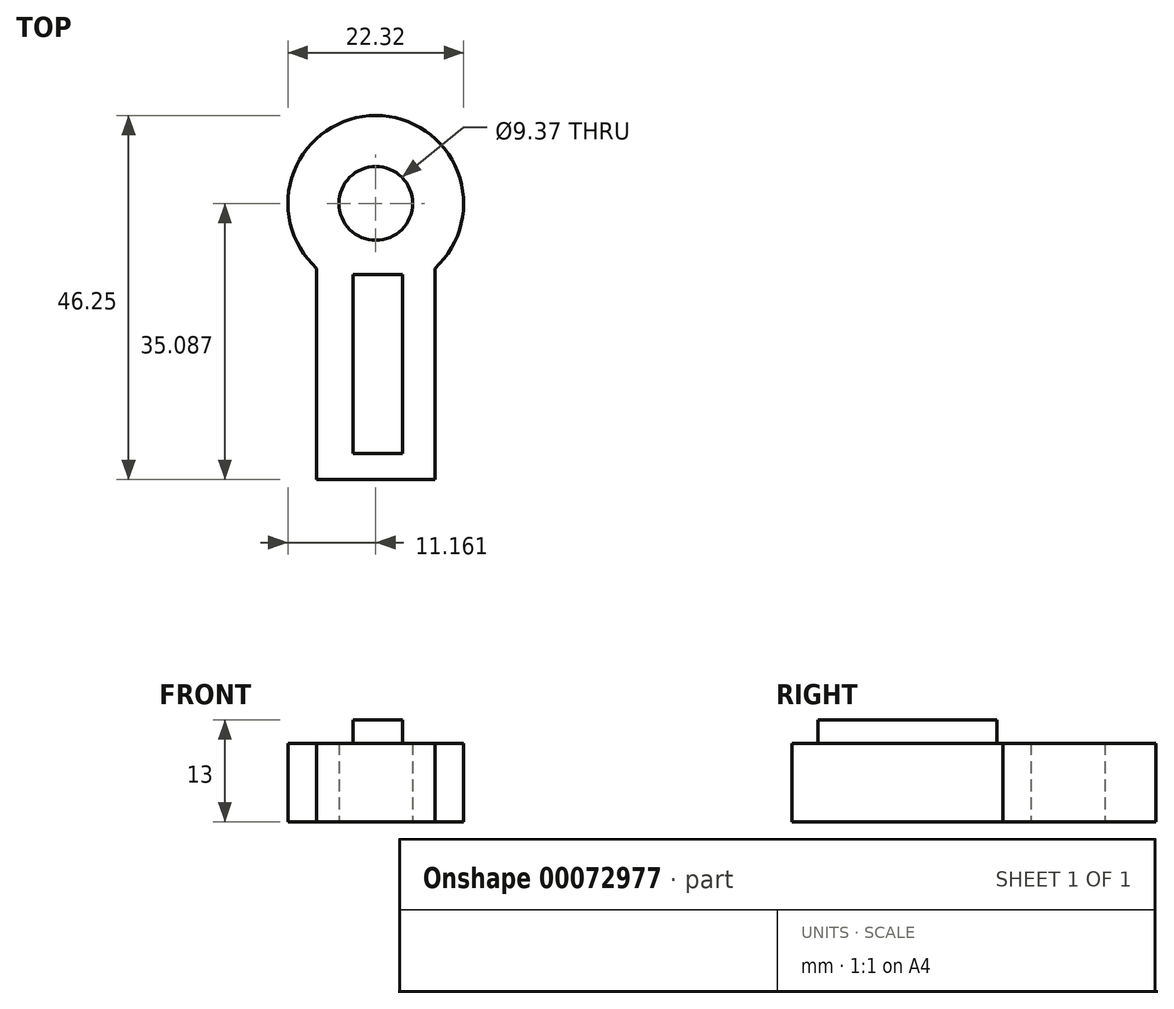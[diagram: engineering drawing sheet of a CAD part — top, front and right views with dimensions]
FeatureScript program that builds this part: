
annotation { "Feature Type Name" : "Feature", "Feature Type Description" : "" }
export const myFeature = defineFeature(function(context is Context, id is Id, definition is map)
    precondition{}
    {
        {
            var Q0;
            Q0=qCreatedBy(makeId("Top.planeOp"),FACE);
            var sketch = newSketch(context, id + "F0", { "sketchPlane" : qUnion([Q0])});
            skArc(sketch, "E0", {"start": v(20.52, 31.4) * mm, "mid": v(13.02, 50.82) * mm, "end": v(5.52, 31.4) * mm});
            skLineSegment(sketch, "E1.top", {"start": v(5.52, 4.57) * mm, "end": v(20.52, 4.57) * mm});
            skLineSegment(sketch, "E1.left", {"start": v(5.52, 31.4) * mm, "end": v(5.52, 4.57) * mm});
            skLineSegment(sketch, "E1.right", {"start": v(20.52, 31.4) * mm, "end": v(20.52, 4.57) * mm});
            skCircle(sketch, "E2", {"center": v(13.02, 39.66) * mm, "radius": 4.68 * mm});
            skLineSegment(sketch, "E3.bottom", {"start": v(10.13, 30.64) * mm, "end": v(16.42, 30.64) * mm});
            skLineSegment(sketch, "E3.top", {"start": v(10.13, 7.89) * mm, "end": v(16.42, 7.89) * mm});
            skLineSegment(sketch, "E3.left", {"start": v(10.13, 30.64) * mm, "end": v(10.13, 7.89) * mm});
            skLineSegment(sketch, "E3.right", {"start": v(16.42, 30.64) * mm, "end": v(16.42, 7.89) * mm});
            skSolve(sketch);
        }
        {
            var Q0;
            Q0=makeQuery(id+"F0.imprint","IMPRINT",FACE,{"disambiguationData":[TD([[makeQuery(id+"F0.imprint","IMPRINT",EDGE,{"derivedFrom":sQuery(id+"F0.wireOp",EDGE,"E0")}),1.0]])]});
            extrude(context, id + "F1", {"entities" : qUnion([Q0]), "depth" : 10 * mm});
        }
        {
            var Q0;
            Q0=makeQuery(id+"F0.imprint","IMPRINT",FACE,{"disambiguationData":[TD([[makeQuery(id+"F0.imprint","IMPRINT",EDGE,{"derivedFrom":sQuery(id+"F0.wireOp",EDGE,"E3.bottom")}),-1.0]])]});
            extrude(context, id + "F2", {"entities" : qUnion([Q0]), "operationType" : NewBodyOperationType.ADD, "depth" : 13 * mm});
        }
    });
